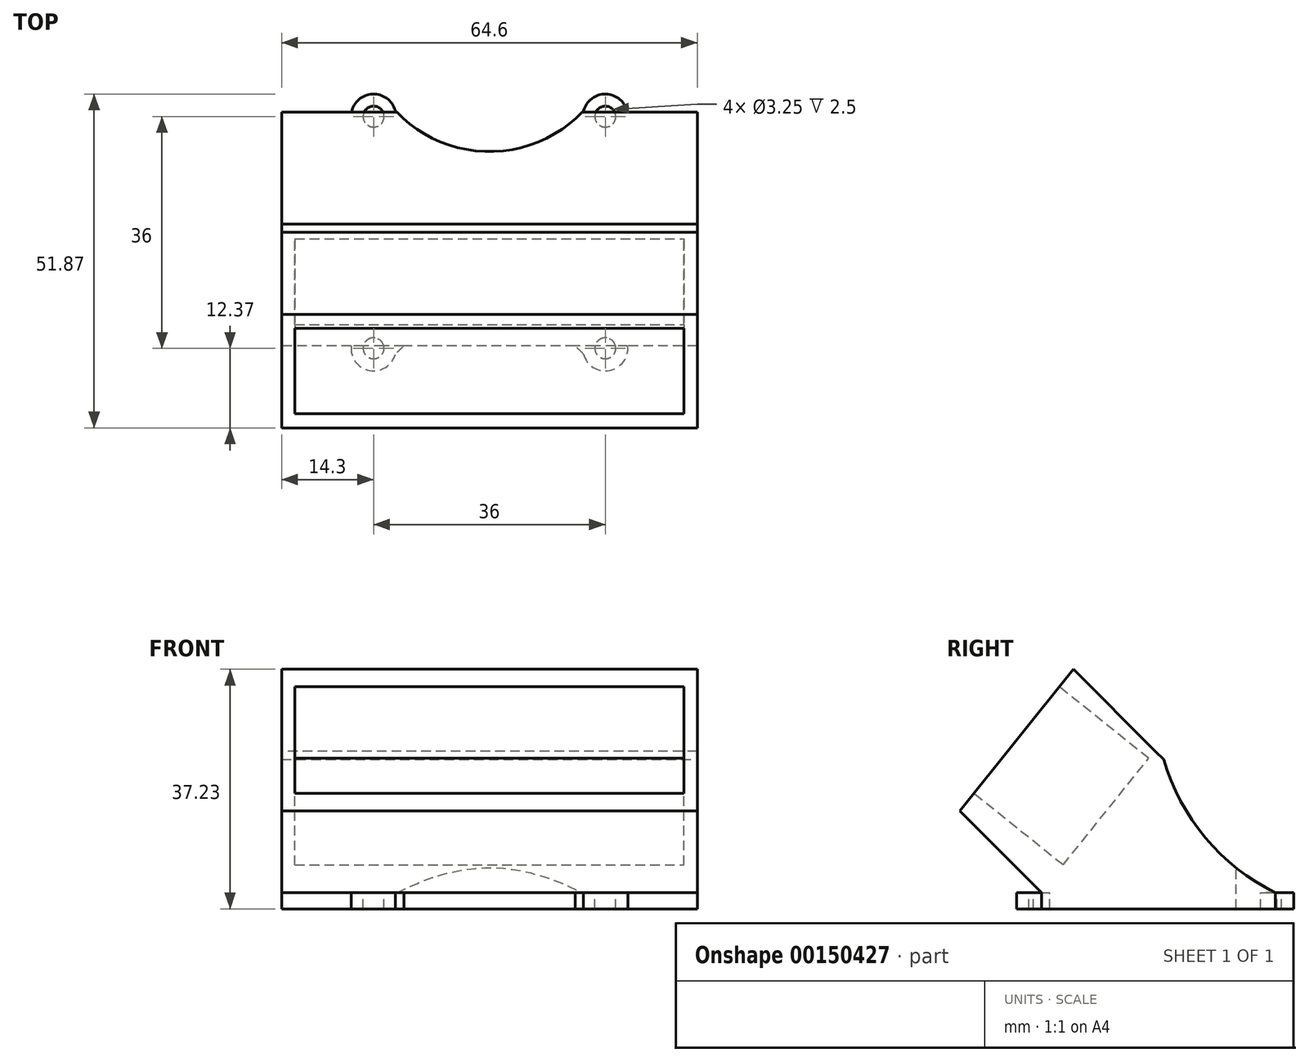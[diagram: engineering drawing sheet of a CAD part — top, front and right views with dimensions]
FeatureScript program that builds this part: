
annotation { "Feature Type Name" : "Feature", "Feature Type Description" : "" }
export const myFeature = defineFeature(function(context is Context, id is Id, definition is map)
    precondition{}
    {
        {
            var Q0;
            Q0=qCreatedBy(makeId("Top.planeOp"),FACE);
            var sketch = newSketch(context, id + "F0", { "sketchPlane" : qUnion([Q0])});
            skLineSegment(sketch, "E0.bottom", {"start": v(-18, -18) * mm, "end": v(18, -18) * mm, "construction": true});
            skLineSegment(sketch, "E0.top", {"start": v(-18, 18) * mm, "end": v(18, 18) * mm, "construction": true});
            skLineSegment(sketch, "E0.left", {"start": v(-18, -18) * mm, "end": v(-18, 18) * mm, "construction": true});
            skLineSegment(sketch, "E0.right", {"start": v(18, -18) * mm, "end": v(18, 18) * mm, "construction": true});
            skPoint(sketch, "E0.middle", {"position": v(0, 0) * mm});
            skCircle(sketch, "E1", {"center": v(18, 18) * mm, "radius": 1.63 * mm});
            skCircle(sketch, "E2.MirrorC", {"center": v(18, -18) * mm, "radius": 1.63 * mm});
            skCircle(sketch, "E3.MirrorC", {"center": v(-18, -18) * mm, "radius": 1.63 * mm});
            skCircle(sketch, "E4.MirrorC", {"center": v(-18, 18) * mm, "radius": 1.63 * mm});
            skCircle(sketch, "E5", {"center": v(-18, 18) * mm, "radius": 3.5 * mm});
            skCircle(sketch, "E6.MirrorC", {"center": v(-18, -18) * mm, "radius": 3.5 * mm});
            skCircle(sketch, "E7.MirrorC", {"center": v(18, 18) * mm, "radius": 3.5 * mm});
            skCircle(sketch, "E8.MirrorC", {"center": v(18, -18) * mm, "radius": 3.5 * mm});
            skArc(sketch, "E9", {"start": v(-14.63, 18.94) * mm, "mid": v(-0.01, 12.57) * mm, "end": v(14.62, 18.91) * mm});
            skArc(sketch, "E10.MirrorCS", {"start": v(-14.63, -18.94) * mm, "mid": v(-0.01, -12.57) * mm, "end": v(14.62, -18.91) * mm});
            skArc(sketch, "E11", {"start": v(-18.78, -14.59) * mm, "mid": v(-12.5, 0.03) * mm, "end": v(-18.87, 14.6) * mm});
            skArc(sketch, "E12.MirrorCS", {"start": v(18.78, -14.59) * mm, "mid": v(12.5, 0.03) * mm, "end": v(18.87, 14.6) * mm});
            skSolve(sketch);
        }
        {
            var Q0;
            Q0=qCreatedBy(makeId("Right.planeOp"),FACE);
            var sketch = newSketch(context, id + "F1", { "sketchPlane" : qUnion([Q0])});
            skLineSegment(sketch, "E13", {"start": v(0, 0) * mm, "end": v(23, 0) * mm, "construction": true});
            skLineSegment(sketch, "E14", {"start": v(10.63, 12.37) * mm, "end": v(15.74, 17.49) * mm, "construction": true});
            skPoint(sketch, "E15.orphan", {"position": v(-1.75, 24.75) * mm});
            skLineSegment(sketch, "E16.0", {"start": v(-17.64, 0) * mm, "end": v(-30.37, 12.73) * mm});
            skLineSegment(sketch, "E17", {"start": v(23, 0) * mm, "end": v(-17.64, 0) * mm});
            skLineSegment(sketch, "E18", {"start": v(0, 22) * mm, "end": v(23, 0) * mm});
            skLineSegment(sketch, "E19", {"start": v(0, 22) * mm, "end": v(-12.73, 34.73) * mm});
            skLineSegment(sketch, "E20", {"start": v(-30.37, 12.73) * mm, "end": v(-12.73, 34.73) * mm});
            skSolve(sketch);
        }
        {
            var Q0;
            Q0=makeQuery(id+"F1.imprint","IMPRINT",FACE,{"disambiguationData":[TD([[makeQuery(id+"F1.imprint","IMPRINT",EDGE,{"derivedFrom":sQuery(id+"F1.wireOp",EDGE,"E16.0")}),-1.0]])]});
            extrude(context, id + "F2", {"entities" : qUnion([Q0]), "depth" : 32.3 * mm});
        }
        {
            var Q0;
            Q0=makeQuery(id+"F2.opExtrude","CAP_FACE",FACE,{"disambiguationData":[OSD([sQuery(id+"F1.wireOp",EDGE,"E16.0"),sQuery(id+"F1.wireOp",EDGE,"E17"),sQuery(id+"F1.wireOp",EDGE,"E18"),sQuery(id+"F1.wireOp",EDGE,"E19"),sQuery(id+"F1.wireOp",EDGE,"E20")])],"isStart":true});
            extrude(context, id + "F3", {"entities" : qUnion([Q0]), "operationType" : NewBodyOperationType.ADD, "depth" : 32.3 * mm});
        }
        {
            var Q0;
            {var subQ0=sQuery(id+"F1.wireOp",EDGE,"E20");Q0=makeQuery(id+"F3.boolean.opBoolean","MERGE",FACE,{"derivedFrom":[makeQuery(id+"F2.opExtrude","SWEPT_FACE",FACE,{"disambiguationData":[OSD([subQ0])]}),makeQuery(id+"F3.opExtrude","SWEPT_FACE",FACE,{"disambiguationData":[OSD([subQ0])]})]});}
            var sketch = newSketch(context, id + "F4", { "sketchPlane" : qUnion([Q0])});
            skLineSegment(sketch, "E21", {"start": v(0, 19.13) * mm, "end": v(0, -9.06) * mm, "construction": true});
            skLineSegment(sketch, "E22.bottom", {"start": v(-30.22, -5.6) * mm, "end": v(30.23, -5.6) * mm});
            skLineSegment(sketch, "E22.top", {"start": v(-30.23, 15.66) * mm, "end": v(30.23, 15.66) * mm});
            skLineSegment(sketch, "E22.left", {"start": v(-30.22, -5.6) * mm, "end": v(-30.23, 15.66) * mm});
            skLineSegment(sketch, "E22.right", {"start": v(30.23, -5.6) * mm, "end": v(30.23, 15.66) * mm});
            skPoint(sketch, "E22.middle", {"position": v(0, 5.03) * mm});
            skSolve(sketch);
        }
        {
            var Q0;
            Q0=makeQuery(id+"F4.imprint","IMPRINT",FACE,{"disambiguationData":[TD([[makeQuery(id+"F4.imprint","IMPRINT",EDGE,{"derivedFrom":sQuery(id+"F4.wireOp",EDGE,"E22.bottom")}),1.0]])]});
            extrude(context, id + "F5", {"entities" : qUnion([Q0]), "operationType" : NewBodyOperationType.REMOVE, "oppositeDirection" : true, "depth" : 17.8 * mm});
        }
        {
            var Q0;
            Q0=makeQuery(id+"F2.opExtrude","CAP_FACE",FACE,{"disambiguationData":[OSD([sQuery(id+"F1.wireOp",EDGE,"E16.0"),sQuery(id+"F1.wireOp",EDGE,"E17"),sQuery(id+"F1.wireOp",EDGE,"E18"),sQuery(id+"F1.wireOp",EDGE,"E19"),sQuery(id+"F1.wireOp",EDGE,"E20")])],"isStart":false});
            var sketch = newSketch(context, id + "F6", { "sketchPlane" : qUnion([Q0])});
            skArc(sketch, "E23", {"start": v(1.32, 20.74) * mm, "mid": v(7.81, 8.54) * mm, "end": v(18.68, 0) * mm});
            skSolve(sketch);
        }
        {
            var Q0;
            Q0=qSketchRegion(id+"F0",true);
            extrude(context, id + "F7", {"entities" : qUnion([Q0]), "operationType" : NewBodyOperationType.ADD, "oppositeDirection" : true, "depth" : 2.5 * mm});
        }
        {
            var Q0;
            {var subQ0=sQuery(id+"F6.wireOp",EDGE,"E23");Q0=makeQuery(id+"F6.imprint","IMPRINT",FACE,{"disambiguationData":[TD([[makeQuery(id+"F6.imprint","IMPRINT",EDGE,{"derivedFrom":subQ0}),1.0]])]});}
            extrude(context, id + "F8", {"entities" : qUnion([Q0]), "operationType" : NewBodyOperationType.REMOVE, "oppositeDirection" : true, "depth" : 125 * mm});
        }
        {
            var Q0;
            {var subQ0=sQuery(id+"F0.wireOp",EDGE,"E9");var subQ1=makeQuery(id+"F7.opExtrude","SWEPT_FACE",FACE,{"disambiguationData":[OSD([subQ0])]});var subQ2=sQuery(id+"F1.wireOp",EDGE,"E17");var subQ9=sQuery(id+"F1.wireOp",EDGE,"E18");Q0=makeQuery(id+"F8.boolean.opBoolean","SPLIT",FACE,{"disambiguationData":[TD([subQ1])],"derivedFrom":makeQuery(id+"F7.boolean.opBoolean","SPLIT",FACE,{"disambiguationData":[TD([makeQuery(id+"F2.opExtrude","SWEPT_FACE",FACE,{"disambiguationData":[OSD([subQ9])]})])],"derivedFrom":makeQuery(id+"F3.boolean.opBoolean","MERGE",FACE,{"derivedFrom":[makeQuery(id+"F2.opExtrude","SWEPT_FACE",FACE,{"disambiguationData":[OSD([subQ2])]}),makeQuery(id+"F3.opExtrude","SWEPT_FACE",FACE,{"disambiguationData":[OSD([subQ2])]})]})})});}
            extrude(context, id + "F9", {"entities" : qUnion([Q0]), "operationType" : NewBodyOperationType.REMOVE, "oppositeDirection" : true, "depth" : 25 * mm});
        }
        {
            var Q0;
            {var subQ2=sQuery(id+"F1.wireOp",EDGE,"E17");var subQ7=sQuery(id+"F0.wireOp",EDGE,"E7.MirrorC");var subQ13=sQuery(id+"F1.wireOp",EDGE,"E18");var subQ17=makeQuery(id+"F7.opExtrude","SWEPT_FACE",FACE,{"disambiguationData":[OSD([subQ7])]});Q0=makeQuery(id+"F8.boolean.opBoolean","SPLIT",FACE,{"disambiguationData":[TD([subQ17])],"derivedFrom":makeQuery(id+"F7.boolean.opBoolean","SPLIT",FACE,{"disambiguationData":[TD([makeQuery(id+"F2.opExtrude","SWEPT_FACE",FACE,{"disambiguationData":[OSD([subQ13])]})])],"derivedFrom":makeQuery(id+"F3.boolean.opBoolean","MERGE",FACE,{"derivedFrom":[makeQuery(id+"F2.opExtrude","SWEPT_FACE",FACE,{"disambiguationData":[OSD([subQ2])]}),makeQuery(id+"F3.opExtrude","SWEPT_FACE",FACE,{"disambiguationData":[OSD([subQ2])]})]})})});}
            var Q1;
            {var subQ6=sQuery(id+"F0.wireOp",EDGE,"E5");var subQ10=sQuery(id+"F1.wireOp",EDGE,"E18");var subQ11=sQuery(id+"F1.wireOp",EDGE,"E17");var subQ16=makeQuery(id+"F7.opExtrude","SWEPT_FACE",FACE,{"disambiguationData":[OSD([subQ6])]});Q1=makeQuery(id+"F8.boolean.opBoolean","SPLIT",FACE,{"disambiguationData":[TD([subQ16])],"derivedFrom":makeQuery(id+"F7.boolean.opBoolean","SPLIT",FACE,{"disambiguationData":[TD([makeQuery(id+"F2.opExtrude","SWEPT_FACE",FACE,{"disambiguationData":[OSD([subQ10])]})])],"derivedFrom":makeQuery(id+"F3.boolean.opBoolean","MERGE",FACE,{"derivedFrom":[makeQuery(id+"F2.opExtrude","SWEPT_FACE",FACE,{"disambiguationData":[OSD([subQ11])]}),makeQuery(id+"F3.opExtrude","SWEPT_FACE",FACE,{"disambiguationData":[OSD([subQ11])]})]})})});}
            var Q2;
            {var subQ1=sQuery(id+"F0.wireOp",EDGE,"E10.MirrorCS");var subQ2=sQuery(id+"F1.wireOp",EDGE,"E17");Q2=makeQuery(id+"F7.boolean.opBoolean","SPLIT",FACE,{"disambiguationData":[TD([makeQuery(id+"F7.opExtrude","SWEPT_FACE",FACE,{"disambiguationData":[OSD([subQ1])]})])],"derivedFrom":makeQuery(id+"F3.boolean.opBoolean","MERGE",FACE,{"derivedFrom":[makeQuery(id+"F2.opExtrude","SWEPT_FACE",FACE,{"disambiguationData":[OSD([subQ2])]}),makeQuery(id+"F3.opExtrude","SWEPT_FACE",FACE,{"disambiguationData":[OSD([subQ2])]})]})});}
            var Q3;
            Q3=makeQuery(id+"F7.opExtrude","CAP_FACE",FACE,{"disambiguationData":[OSD([sQuery(id+"F0.wireOp",EDGE,"E1"),sQuery(id+"F0.wireOp",EDGE,"E2.MirrorC"),sQuery(id+"F0.wireOp",EDGE,"E3.MirrorC"),sQuery(id+"F0.wireOp",EDGE,"E4.MirrorC"),sQuery(id+"F0.wireOp",EDGE,"E5"),sQuery(id+"F0.wireOp",EDGE,"E6.MirrorC"),sQuery(id+"F0.wireOp",EDGE,"E7.MirrorC"),sQuery(id+"F0.wireOp",EDGE,"E8.MirrorC"),sQuery(id+"F0.wireOp",EDGE,"E9"),sQuery(id+"F0.wireOp",EDGE,"E10.MirrorCS"),sQuery(id+"F0.wireOp",EDGE,"E11"),sQuery(id+"F0.wireOp",EDGE,"E12.MirrorCS")])],"isStart":false});
            extrude(context, id + "F10", {"entities" : qUnion([Q0, Q1, Q2]), "operationType" : NewBodyOperationType.ADD, "endBound" : BoundingType.UP_TO_SURFACE, "endBoundEntityFace" : qUnion([Q3]), "depth" : 25 * mm});
        }
    });
